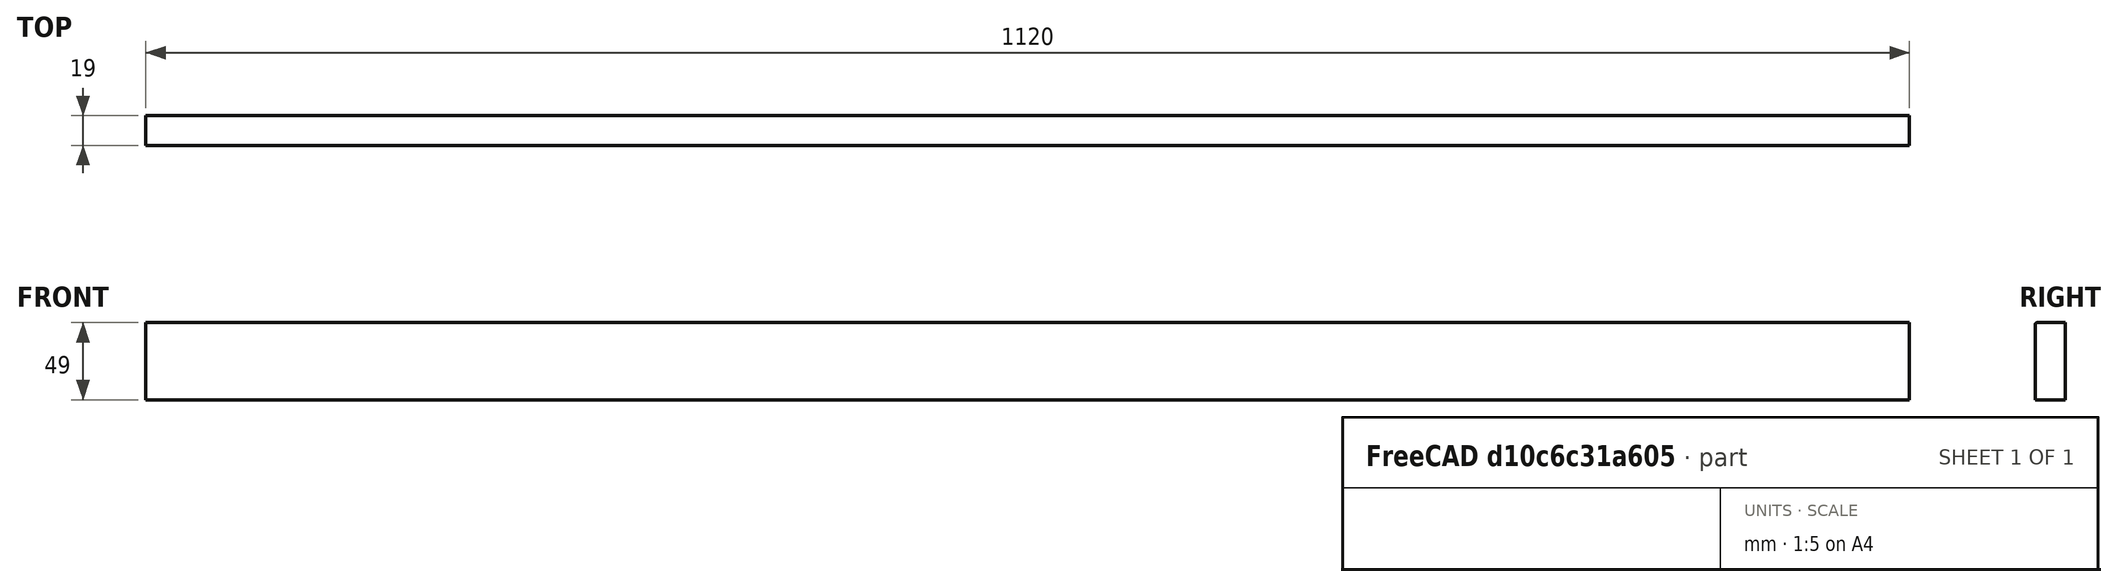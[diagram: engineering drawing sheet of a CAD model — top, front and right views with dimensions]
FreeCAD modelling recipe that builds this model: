
FCSTD DOCUMENT  (FreeCAD 0.18.3R)
Label: TraverseAvantConsole
License: All rights reserved
LicenseURL: http://en.wikipedia.org/wiki/All_rights_reserved
objects: Drawing::FeatureViewPython×4, Drawing::FeatureViewPart×2, Part::Box×1, Part::Fillet×1, Drawing::FeaturePage×1
note: 2 computed .brp shape members not serialized (recipe doc carries the construction recipe); baked Part::Feature solids carry a one-line shape summary decoded from their .brp

FEATURE [Part::Box] Box  label="Cube"
  AttacherType = Attacher::AttachEngine3D
  Height = 49
  Length = 1120
  Width = 19
FEATURE [Part::Fillet] Fillet
  Base = -> Box
  Edges = 1 edges r=1: [Edge10]
FEATURE [Drawing::FeatureViewPart] Ortho  label="Ortho_0_0"
  Direction = (0,0,1)
  HiddenWidth = 0.15
  LineWidth = 0.35
  Rotation = 0
  Scale = 0.2
  ShowHiddenLines = false
  ShowSmoothLines = true
  Source = -> Fillet
  Tolerance = 0.05
  ViewResult = <g id="Ortho_0_0"\n   transform="rotate(0,36.5,115.6) translate(36.5,115.6) scale(0.2,0.2)"\n  >\n<g   fill="none"\n   stroke="rgb(0, 0, 0)"\n   stroke-linecap="butt"\n   stroke-linejoin="miter"\n   stroke-width="1.750000"\n   transform="scale(1,-1)"\n  >\n<path d="M0,-2.22045e-16 C0,0.00209593 0,0.00419186 0,0.00628779  C0,0.0125492 0,0.0188107 0,0.0250721  C0,0.0354203 0,0.0457685 0,0.0561167  C0,0.0704215 0,0.0847263 0,0.0990311  C0,0.117113 0,0.135194 0,0.153276  C0,0.174907 0,0.196538 0,0.218169  C0,0.243077 0,0.267985 0,0.292893  C0,0.320766 0,0.348638 0,0.37651  C0,0.436231 0,0.499433 0,0.566116  C0,0.701837 0,0.850207 0,1 " /><path id= "2" d=" M 0 1 L 0 19 " />\n<path id= "3" d=" M 0 -2.22045e-16 L 1120 -2.22045e-16 " />\n<path d="M1120,-2.22045e-16 C1120,0.00209593 1120,0.00419186 1120,0.00628779  C1120,0.0125492 1120,0.0188107 1120,0.0250721  C1120,0.0354203 1120,0.0457685 1120,0.0561167  C1120,0.0704215 1120,0.0847263 1120,0.0990311  C1120,0.117113 1120,0.135194 1120,0.153276  C1120,0.174907 1120,0.196538 1120,0.218169  C1120,0.243077 1120,0.267985 1120,0.292893  C1120,0.320766 1120,0.348638 1120,0.37651  C1120,0.436231 1120,0.499433 1120,0.566116  C1120,0.701837 1120,0.850207 1120,1 " /><path id= "5" d=" M 0 19 L 1120 19 " />\n<path id= "6" d=" M 1120 1 L 1120 19 " />\n</g>\n<g   fill="none"\n   stroke="rgb(0, 0, 0)"\n   stroke-linecap="butt"\n   stroke-linejoin="miter"\n   stroke-width="1.750000"\n   transform="scale(1,-1)"\n  >\n<path id= "1" d=" M 0 1 L 1120 1 " />\n</g>\n</g>
  Visible = false
  X = 36.5
  Y = 115.6
FEATURE [Drawing::FeatureViewPart] Ortho002  label="Ortho_0_1"
  Direction = (0,-1,0)
  HiddenWidth = 0.15
  LineWidth = 0.35
  Rotation = 90
  Scale = 0.2
  ShowHiddenLines = false
  ShowSmoothLines = true
  Source = -> Fillet
  Tolerance = 0.05
  ViewResult = <g id="Ortho_0_1"\n   transform="rotate(90,36.5,65.6) translate(36.5,65.6) scale(0.2,0.2)"\n  >\n<g   fill="none"\n   stroke="rgb(0, 0, 0)"\n   stroke-linecap="butt"\n   stroke-linejoin="miter"\n   stroke-width="1.750000"\n   transform="scale(1,-1)"\n  >\n<path id= "1" d=" M 0 0 L -48 0 " />\n<path d="M-48,0 Q-48.1694,0 -48.3303,0  Q-48.4354,0 -48.532,0  Q-48.6257,0 -48.7071,0  Q-48.7445,0 -48.7818,0  Q-48.8143,0 -48.8467,0  Q-48.8738,0 -48.901,0  Q-48.9224,0 -48.9439,0  Q-48.9594,0 -48.9749,0  Q-48.9843,0 -48.9937,0  Q-48.9969,0 -49,0 " /><path id= "3" d=" M 0 1120 L -48 1120 " />\n<path id= "4" d=" M 0 0 L 0 1120 " />\n<path id= "5" d=" M -49 0 L -49 1120 " />\n<path d="M-48,1120 Q-48.1694,1120 -48.3303,1120  Q-48.4354,1120 -48.532,1120  Q-48.6257,1120 -48.7071,1120  Q-48.7445,1120 -48.7818,1120  Q-48.8143,1120 -48.8467,1120  Q-48.8738,1120 -48.901,1120  Q-48.9224,1120 -48.9439,1120  Q-48.9594,1120 -48.9749,1120  Q-48.9843,1120 -48.9937,1120  Q-48.9969,1120 -49,1120 " /></g>\n<g   fill="none"\n   stroke="rgb(0, 0, 0)"\n   stroke-linecap="butt"\n   stroke-linejoin="miter"\n   stroke-width="1.750000"\n   transform="scale(1,-1)"\n  >\n<path id= "1" d=" M -48 0 L -48 1120 " />\n</g>\n</g>
  Visible = false
  X = 36.5
  Y = 65.6
FEATURE [Drawing::FeatureViewPython] dim001  # drawing view (typed FeaturePython)
  Rotation = 0
  ViewResult = <g> \n  <line x1="36.500000" y1="54.000000" x2="36.500000" y2="37.330435" style="stroke:rgb(0,0,255);stroke-width:0.30" />\n<line x1="260.500000" y1="54.000000" x2="260.500000" y2="37.330435" style="stroke:rgb(0,0,255);stroke-width:0.30" />\n<line x1="36.500000" y1="38.330435" x2="260.500000" y2="38.330435" style="stroke:rgb(0,0,255);stroke-width:0.30" /> \n  <polygon points="260.500000,38.330435 257.500000,37.330435 256.500000,38.330435 257.500000,39.330435" style="fill:rgb(0,0,255);stroke:rgb(0,0,255);stroke-width:0" /><polygon points="36.500000,38.330435 39.500000,39.330435 40.500000,38.330435 39.500000,37.330435" style="fill:rgb(0,0,255);stroke:rgb(0,0,255);stroke-width:0" /> \n  <text x="148.500000" y="36.330435" font-family="Verdana" font-size="3.6" fill="rgb(0,0,255)" text-anchor="middle" transform="rotate(0.000000 148.500000,36.330435)" >1120</text> </g>
  Visible = true
  X = 0
  Y = 0
  arrowL1 = 3
  arrowL2 = 1
  arrowW = 2
  arrow_scheme = 0
  autoPlaceOffset = 2
  autoPlaceText = true
  click1_x = 155
  click1_y = 38.3304
  click2_x = 155
  click2_y = 38.3304
  comma_decimal_place = false
  dimension_line_overshoot = 1
  gap_datum_points = 2
  halfDimension_linear = false
  lineColor = rgb(0,0,255)
  strokeWidth = 0.3
  textFormat_linear = %(value)3.0f
  textRenderer_color = rgb(0,0,255)
  textRenderer_family = Verdana
  textRenderer_size = 3.6
  unit_custom_scale = 1
  unit_scheme = 0
FEATURE [Drawing::FeatureViewPython] dim003  # drawing view (typed FeaturePython)
  Rotation = 0
  ViewResult = <g> \n  <line x1="262.500000" y1="111.800000" x2="276.000000" y2="111.800000" style="stroke:rgb(0,0,255);stroke-width:0.30" />\n<line x1="262.500000" y1="115.580194" x2="276.000000" y2="115.580194" style="stroke:rgb(0,0,255);stroke-width:0.30" />\n<line x1="275.000000" y1="111.800000" x2="275.000000" y2="115.580194" style="stroke:rgb(0,0,255);stroke-width:0.30" /> \n  <polygon points="275.000000,115.580194 274.000000,118.580194 275.000000,119.580194 276.000000,118.580194" style="fill:rgb(0,0,255);stroke:rgb(0,0,255);stroke-width:0" /><polygon points="275.000000,111.800000 276.000000,108.800000 275.000000,107.800000 274.000000,108.800000" style="fill:rgb(0,0,255);stroke:rgb(0,0,255);stroke-width:0" /> \n  <text x="273.000000" y="113.690097" font-family="Verdana" font-size="3.6" fill="rgb(0,0,255)" text-anchor="middle" transform="rotate(-90.000000 273.000000,113.690097)" > 19</text> </g>
  Visible = true
  X = 0
  Y = 0
  arrowL1 = 3
  arrowL2 = 1
  arrowW = 2
  arrow_scheme = 0
  autoPlaceOffset = 2
  autoPlaceText = true
  click1_x = 275
  click1_y = 109.689
  click2_x = 275
  click2_y = 109.689
  comma_decimal_place = false
  dimension_line_overshoot = 1
  gap_datum_points = 2
  halfDimension_linear = false
  lineColor = rgb(0,0,255)
  strokeWidth = 0.3
  textFormat_linear = %(value)3.0f
  textRenderer_color = rgb(0,0,255)
  textRenderer_family = Verdana
  textRenderer_size = 3.6
  unit_custom_scale = 1
  unit_scheme = 0
FEATURE [Drawing::FeatureViewPython] noteCircle001  # drawing view (typed FeaturePython)
  Rotation = 0
  ViewResult = <g> <line x1="160.000000" y1="130.800000" x2="148.500000" y2="115.400000" style="stroke:rgb(0,0,255);stroke-width:0.30" />\n<line x1="160.000000" y1="130.800000" x2="175.000000" y2="130.800000" style="stroke:rgb(0,0,255);stroke-width:0.30" />\n <circle cx ="175.000000" cy ="130.800000" r="4.500000" stroke="rgb(0,0,255)" fill="rgb(255,255,255)" /> \n<text x="173.500000" y="132.300000" font-family="inherit" font-size="5" fill="rgb(0,150,0)" text-anchor="inherit"  >1</text> </g>
  Visible = true
  X = 0
  Y = 0
  click1_x = 160
  click1_y = 130.8
  click2_x = 175
  click2_y = 130.8
  lineColor = rgb(0,0,255)
  noteCircle_fill = rgb(255,255,255)
  noteCircle_radius = 4.5
  noteText = 1
  strokeWidth = 0.3
  textRenderer_noteCircle_color = rgb(0,150,0)
  textRenderer_noteCircle_family = inherit
  textRenderer_noteCircle_size = 5
FEATURE [Drawing::FeatureViewPython] dim002  # drawing view (typed FeaturePython)
  Rotation = 0
  ViewResult = <g> \n  <line x1="262.500000" y1="55.801260" x2="276.000000" y2="55.801260" style="stroke:rgb(0,0,255);stroke-width:0.30" />\n<line x1="262.500000" y1="65.600000" x2="276.000000" y2="65.600000" style="stroke:rgb(0,0,255);stroke-width:0.30" />\n<line x1="275.000000" y1="55.801260" x2="275.000000" y2="65.600000" style="stroke:rgb(0,0,255);stroke-width:0.30" /> \n  <polygon points="275.000000,65.600000 274.000000,68.600000 275.000000,69.600000 276.000000,68.600000" style="fill:rgb(0,0,255);stroke:rgb(0,0,255);stroke-width:0" /><polygon points="275.000000,55.801260 276.000000,52.801260 275.000000,51.801260 274.000000,52.801260" style="fill:rgb(0,0,255);stroke:rgb(0,0,255);stroke-width:0" /> \n  <text x="273.000000" y="60.700630" font-family="Verdana" font-size="3.6" fill="rgb(0,0,255)" text-anchor="middle" transform="rotate(-90.000000 273.000000,60.700630)" > 49</text> </g>
  Visible = true
  X = 0
  Y = 0
  arrowL1 = 3
  arrowL2 = 1
  arrowW = 2
  arrow_scheme = 0
  autoPlaceOffset = 2
  autoPlaceText = true
  click1_x = 275
  click1_y = 59.6348
  click2_x = 275
  click2_y = 59.6348
  comma_decimal_place = false
  dimension_line_overshoot = 1
  gap_datum_points = 2
  halfDimension_linear = false
  lineColor = rgb(0,0,255)
  strokeWidth = 0.3
  textFormat_linear = %(value)3.0f
  textRenderer_color = rgb(0,0,255)
  textRenderer_family = Verdana
  textRenderer_size = 3.6
  unit_custom_scale = 1
  unit_scheme = 0
FEATURE [Drawing::FeaturePage] Page
  EditableTexts = GB | Traverse avant console | 1 : congé rayon 1mm | A4 | X / Y | 2/10 | PN | DN | 08/04/2018 | REV A
  Group = -> [Ortho,Ortho002,dim001,dim003,noteCircle001,dim002]
  Template = <path>
note: 1 file-system path scrubbed to <path> (originals preserved in the JSON sidecar)
